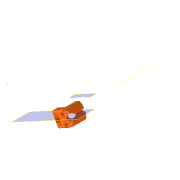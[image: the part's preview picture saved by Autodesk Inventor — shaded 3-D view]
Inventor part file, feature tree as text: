
AUTODESK INVENTOR PART (.ipt)
format: ipt  version: 2022.5 (Build 265521000, 521)  size: 467,456 bytes
history: native  units: in
note: dims shown in document units (in); Inventor stores cm internally (conversion verified against a paired STEP export)
features: extrude x9, other x8, sketch x8, reference x8, projected_geometry x3, plane x2, fillet x2, hole x2
ambient origin geometry x8: Origin, YZ Plane, XZ Plane, XY Plane, X Axis, Y Axis, Z Axis, Center Point
bodies: Solid1 (feature_tree)
feature tree (42):
  plane  "Work Plane1"
  extrude  "Extrusion1"  Depth=1.1811in
  plane  "Arbeitsebene3"
  other  "Arbeitsachse1"
  extrude  "Extrusion17"  TaperAngle=135.0deg  [1 undecoded]
  fillet  "Rundung4"  Radius=0.1575in
  hole  "Bohrung1"  [1 undecoded]
  extrude  "Extrusion19"  Depth=0.5906in
  hole  "Bohrung2"  [1 undecoded]
  extrude  "Extrusion20"  Depth=0.1181in
  extrude  "Extrusion21"  Depth=1.1811in
  extrude  "Extrusion22"  TaperAngle=0.0deg  [1 undecoded]
  fillet  "Rundung6"  Radius=0.4921in
  extrude  "Extrusion23"  Depth=0.1575in
  extrude  "Extrusion24"  TaperAngle=0.0deg  [1 undecoded]
  extrude  "Extrusion25"  Depth=0.3937in TaperAngle=0.0deg
  sketch  "Sketch1"  dims[d0=1.1811in d1=0.0in d22=0.5307in]
  reference  "Reference1"
  reference  "Referenz6"
  reference  "Referenz7"
  reference  "Referenz8"
  sketch  "Skizze22"  dims[d23=0.2653in d25=135.0deg d26=0.1575in]
  projected_geometry  "Projizierte Kontur13"
  projected_geometry  "Projizierte Kontur14"
  sketch  "Skizze24"  dims[d27=0.2362in d29=0.3937in]
  reference  "Referenz9"
  reference  "Referenz10"
  sketch  "Skizze25"  dims[d31=0.5906in d40=0.0591in]
  sketch  "Skizze26"  dims[d42=1.378in d70=0.4724in]
  reference  "Referenz11"
  reference  "Referenz12"
  sketch  "Skizze28"  dims[d71=0.0in d72=-0.0069in d73=0.1181in]
  projected_geometry  "Projizierte Kontur15"
  sketch  "Skizze29"  dims[d74=0.126in d75=0.2362in d76=0.2756in d77=1.1811in d78=90.0deg d79=0.315in d80=0.8108in d84=0.1102in]
  sketch  "Skizze30"  dims[d85=0.1102in d86=0.0in d87=0.0in d88=0.4921in d89=0.4921in d90=0.2362in d91=0.1575in d92=0.0787in d93=90.0deg d94=0.5118in d95=0.8108in d96=0.1575in d97=0.0in d98=0.0in d100=0.3937in d101=0.0in d102=0.0in d103=0.0in d104=0.1575in d105=0.6299in d106=0.6299in d107=0.1181in d108=0.1102in d109=0.1102in d110=0.0in d111=0.0in d112=45.0deg d113=0.0in d114=0.0in d115=0.1102in d116=0.1102in d117=0.3937in d118=0.0in]
  other  "<userpath>\Documents\Matchboxscope\INVENTOR\Matchboxscope_v0.iam"
  other  "Matchboxscope_v0.iam"
  other  "Matchboxscope_sample_v0:1"
  other  "Assembly_Matchboxscope_injectionmolded.iam"
  other  "IM_Matchboxscope_base_old:1"
  other  "IM_Matchboxscope_plate:2"
  other  "DIN 912 - ersetzt durch DIN EN ISO 4762 M3 x 25:2"
note: 5 required parameter values undecoded (feature->parameter linkage not recoverable at this tier; creation-order binding heuristic only, values carry confidence <= 0.55)
